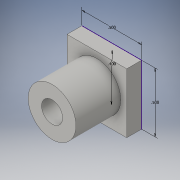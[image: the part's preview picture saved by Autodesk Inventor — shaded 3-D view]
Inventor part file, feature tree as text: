
AUTODESK INVENTOR PART (.ipt)
format: ipt  version: 2016 (Build 200138000, 138)  size: 108,032 bytes
history: native  units: in
note: dims shown in document units (in); Inventor stores cm internally (conversion verified against a paired STEP export)
features: extrude x3, sketch x2
ambient origin geometry x8: Origin, YZ Plane, XZ Plane, XY Plane, X Axis, Y Axis, Z Axis, Center Point
bodies: Solid1 (feature_tree)
feature tree (5):
  sketch  "Sketch1"  dims[d0=0.5in d1=0.5in]
  extrude  "Extrusion1"  Depth=0.5in
  extrude  "Extrusion2"  Depth=0.125in TaperAngle=0.0deg
  extrude  "Extrusion3"  Depth=0.5in TaperAngle=0.0deg
  sketch  "Sketch2"  dims[d2=0.4in d3=0.125in d4=0.0in d5=0.5in d6=0.0in d7=1.0in d8=0.0in]
